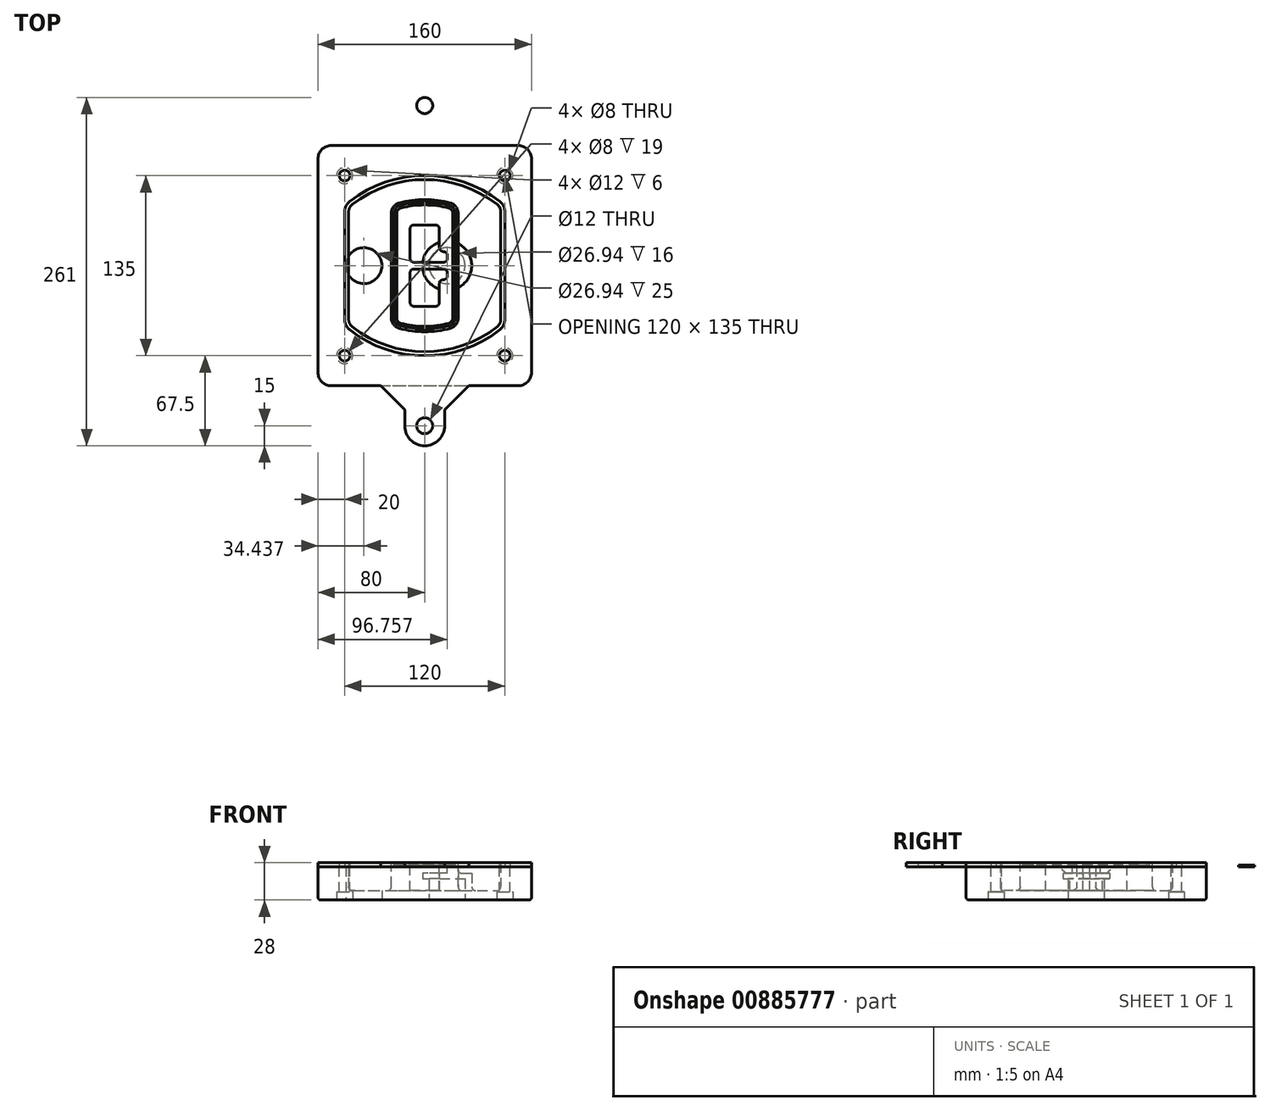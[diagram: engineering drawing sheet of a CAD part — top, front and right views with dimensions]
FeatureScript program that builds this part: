
annotation { "Feature Type Name" : "Feature", "Feature Type Description" : "" }
export const myFeature = defineFeature(function(context is Context, id is Id, definition is map)
    precondition{}
    {
        {
            var Q0;
            Q0=qCreatedBy(makeId("Top.planeOp"),FACE);
            var sketch = newSketch(context, id + "F0", { "sketchPlane" : qUnion([Q0])});
            skPoint(sketch, "E0.rect.middle", {"position": v(0, 0) * mm});
            skLineSegment(sketch, "E1.bottom", {"start": v(-70, -90) * mm, "end": v(70, -90) * mm});
            skLineSegment(sketch, "E1.top", {"start": v(-70, 90) * mm, "end": v(70, 90) * mm});
            skLineSegment(sketch, "E1.left", {"start": v(-80, -80) * mm, "end": v(-80, 80) * mm});
            skLineSegment(sketch, "E1.right", {"start": v(80, -80) * mm, "end": v(80, 80) * mm});
            skLineSegment(sketch, "E2", {"start": v(-80, 90) * mm, "end": v(80, -90) * mm, "construction": true});
            skLineSegment(sketch, "E3", {"start": v(80, 90) * mm, "end": v(-80, -90) * mm, "construction": true});
            skCircle(sketch, "E4", {"center": v(-60, 67.5) * mm, "radius": 4 * mm});
            skCircle(sketch, "E5", {"center": v(60, 67.5) * mm, "radius": 4 * mm});
            skCircle(sketch, "E6", {"center": v(60, -67.5) * mm, "radius": 4 * mm});
            skCircle(sketch, "E7", {"center": v(-60, -67.5) * mm, "radius": 4 * mm});
            skLineSegment(sketch, "E8", {"start": v(-60, 67.5) * mm, "end": v(60, 67.5) * mm, "construction": true});
            skLineSegment(sketch, "E9", {"start": v(60, 67.5) * mm, "end": v(60, -67.5) * mm, "construction": true});
            skLineSegment(sketch, "E10", {"start": v(60, -67.5) * mm, "end": v(-60, -67.5) * mm, "construction": true});
            skLineSegment(sketch, "E11", {"start": v(-60, -67.5) * mm, "end": v(-60, 67.5) * mm, "construction": true});
            skLineSegment(sketch, "E12", {"start": v(-60, 40.3) * mm, "end": v(-60, -40.3) * mm});
            skLineSegment(sketch, "E13", {"start": v(60, 40.3) * mm, "end": v(60, -40.3) * mm});
            skArc(sketch, "E14", {"start": v(56.15, 48.18) * mm, "mid": v(0, 67.5) * mm, "end": v(-56.15, 48.18) * mm});
            skArc(sketch, "E15", {"start": v(-56.15, -48.18) * mm, "mid": v(0, -67.5) * mm, "end": v(56.15, -48.18) * mm});
            skLineSegment(sketch, "E16", {"start": v(-60, 0) * mm, "end": v(60, 0) * mm, "construction": true});
            skPoint(sketch, "E17.visualSharp", {"position": v(-60, -45) * mm});
            skArc(sketch, "E17.filletArc", {"start": v(-60, -40.3) * mm, "mid": v(-58.99, -44.68) * mm, "end": v(-56.15, -48.18) * mm});
            skPoint(sketch, "E18.visualSharp", {"position": v(-60, 45) * mm});
            skArc(sketch, "E18.filletArc", {"start": v(-56.15, 48.18) * mm, "mid": v(-58.99, 44.68) * mm, "end": v(-60, 40.3) * mm});
            skPoint(sketch, "E19.visualSharp", {"position": v(60, 45) * mm});
            skArc(sketch, "E19.filletArc", {"start": v(60, 40.3) * mm, "mid": v(58.99, 44.68) * mm, "end": v(56.15, 48.18) * mm});
            skPoint(sketch, "E20.visualSharp", {"position": v(60, -45) * mm});
            skArc(sketch, "E20.filletArc", {"start": v(56.15, -48.18) * mm, "mid": v(58.99, -44.68) * mm, "end": v(60, -40.3) * mm});
            skPoint(sketch, "E21.visualSharp", {"position": v(-80, 90) * mm});
            skArc(sketch, "E21.filletArc", {"start": v(-70, 90) * mm, "mid": v(-77.07, 87.07) * mm, "end": v(-80, 80) * mm});
            skPoint(sketch, "E22.visualSharp", {"position": v(80, 90) * mm});
            skArc(sketch, "E22.filletArc", {"start": v(80, 80) * mm, "mid": v(77.07, 87.07) * mm, "end": v(70, 90) * mm});
            skPoint(sketch, "E23.visualSharp", {"position": v(80, -90) * mm});
            skArc(sketch, "E23.filletArc", {"start": v(70, -90) * mm, "mid": v(77.07, -87.07) * mm, "end": v(80, -80) * mm});
            skPoint(sketch, "E24.visualSharp", {"position": v(-80, -90) * mm});
            skArc(sketch, "E24.filletArc", {"start": v(-80, -80) * mm, "mid": v(-77.07, -87.07) * mm, "end": v(-70, -90) * mm});
            skArc(sketch, "E25.0", {"start": v(57, 40.3) * mm, "mid": v(56.3, 43.36) * mm, "end": v(54.3, 45.81) * mm});
            skLineSegment(sketch, "E25.1", {"start": v(57, 40.3) * mm, "end": v(57, -40.3) * mm});
            skArc(sketch, "E25.2", {"start": v(54.3, -45.81) * mm, "mid": v(56.3, -43.36) * mm, "end": v(57, -40.3) * mm});
            skArc(sketch, "E25.3", {"start": v(-54.3, -45.81) * mm, "mid": v(0, -64.5) * mm, "end": v(54.3, -45.81) * mm});
            skArc(sketch, "E25.4", {"start": v(-57, -40.3) * mm, "mid": v(-56.3, -43.36) * mm, "end": v(-54.3, -45.81) * mm});
            skArc(sketch, "E25.5", {"start": v(54.3, 45.81) * mm, "mid": v(0, 64.5) * mm, "end": v(-54.3, 45.81) * mm});
            skLineSegment(sketch, "E25.6", {"start": v(-57, 40.3) * mm, "end": v(-57, -40.3) * mm});
            skArc(sketch, "E25.7", {"start": v(-54.3, 45.81) * mm, "mid": v(-56.3, 43.36) * mm, "end": v(-57, 40.3) * mm});
            skArc(sketch, "E26.0", {"start": v(-58.62, 51.33) * mm, "mid": v(-62.58, 46.43) * mm, "end": v(-64, 40.3) * mm});
            skArc(sketch, "E26.1", {"start": v(58.62, 51.33) * mm, "mid": v(0, 71.5) * mm, "end": v(-58.62, 51.33) * mm});
            skArc(sketch, "E26.2", {"start": v(64, 40.3) * mm, "mid": v(62.58, 46.43) * mm, "end": v(58.62, 51.33) * mm});
            skLineSegment(sketch, "E26.3", {"start": v(64, 40.3) * mm, "end": v(64, -40.3) * mm});
            skArc(sketch, "E26.4", {"start": v(58.62, -51.33) * mm, "mid": v(62.58, -46.43) * mm, "end": v(64, -40.3) * mm});
            skLineSegment(sketch, "E26.5", {"start": v(-64, 40.3) * mm, "end": v(-64, -40.3) * mm});
            skArc(sketch, "E26.6", {"start": v(-58.62, -51.33) * mm, "mid": v(0, -71.5) * mm, "end": v(58.62, -51.33) * mm});
            skArc(sketch, "E26.7", {"start": v(-64, -40.3) * mm, "mid": v(-62.58, -46.43) * mm, "end": v(-58.62, -51.33) * mm});
            skSolve(sketch);
        }
        {
            var Q0;
            Q0=makeQuery(id+"F0.imprint","IMPRINT",FACE,{"disambiguationData":[TD([[makeQuery(id+"F0.imprint","IMPRINT",EDGE,{"derivedFrom":sQuery(id+"F0.wireOp",EDGE,"E1.bottom")}),1.0]])]});
            var Q1;
            Q1=makeQuery(id+"F0.imprint","IMPRINT",FACE,{"disambiguationData":[TD([[makeQuery(id+"F0.imprint","IMPRINT",EDGE,{"derivedFrom":sQuery(id+"F0.wireOp",EDGE,"E12")}),1.0]])]});
            var Q2;
            Q2=makeQuery(id+"F0.imprint","IMPRINT",FACE,{"disambiguationData":[TD([[makeQuery(id+"F0.imprint","IMPRINT",EDGE,{"derivedFrom":sQuery(id+"F0.wireOp",EDGE,"E25.0")}),1.0]])]});
            var Q3;
            Q3=makeQuery(id+"F0.imprint","IMPRINT",FACE,{"disambiguationData":[TD([[makeQuery(id+"F0.imprint","IMPRINT",EDGE,{"derivedFrom":sQuery(id+"F0.wireOp",EDGE,"E12")}),-1.0]])]});
            extrude(context, id + "F1", {"entities" : qUnion([Q0, Q1, Q2, Q3]), "oppositeDirection" : true, "depth" : 25 * mm});
        }
        {
            var Q0;
            Q0=makeQuery(id+"F0.imprint","IMPRINT",FACE,{"disambiguationData":[TD([[makeQuery(id+"F0.imprint","IMPRINT",EDGE,{"derivedFrom":sQuery(id+"F0.wireOp",EDGE,"E12")}),1.0]])]});
            extrude(context, id + "F2", {"entities" : qUnion([Q0]), "operationType" : NewBodyOperationType.ADD, "depth" : 3 * mm});
        }
        {
            var Q0;
            Q0=makeQuery(id+"F0.imprint","IMPRINT",FACE,{"disambiguationData":[TD([[makeQuery(id+"F0.imprint","IMPRINT",EDGE,{"derivedFrom":sQuery(id+"F0.wireOp",EDGE,"E25.0")}),1.0]])]});
            extrude(context, id + "F3", {"entities" : qUnion([Q0]), "operationType" : NewBodyOperationType.REMOVE, "oppositeDirection" : true, "depth" : 18 * mm});
        }
        {
            var Q0;
            Q0=makeQuery(id+"F2.opExtrude","CAP_FACE",FACE,{"disambiguationData":[OSD([sQuery(id+"F0.wireOp",EDGE,"E12"),sQuery(id+"F0.wireOp",EDGE,"E13"),sQuery(id+"F0.wireOp",EDGE,"E14"),sQuery(id+"F0.wireOp",EDGE,"E15"),sQuery(id+"F0.wireOp",EDGE,"E17.filletArc"),sQuery(id+"F0.wireOp",EDGE,"E18.filletArc"),sQuery(id+"F0.wireOp",EDGE,"E19.filletArc"),sQuery(id+"F0.wireOp",EDGE,"E20.filletArc"),sQuery(id+"F0.wireOp",EDGE,"E25.0"),sQuery(id+"F0.wireOp",EDGE,"E25.1"),sQuery(id+"F0.wireOp",EDGE,"E25.2"),sQuery(id+"F0.wireOp",EDGE,"E25.3"),sQuery(id+"F0.wireOp",EDGE,"E25.4"),sQuery(id+"F0.wireOp",EDGE,"E25.5"),sQuery(id+"F0.wireOp",EDGE,"E25.6"),sQuery(id+"F0.wireOp",EDGE,"E25.7")])],"isStart":false});
            var sketch = newSketch(context, id + "F4", { "sketchPlane" : qUnion([Q0])});
            skArc(sketch, "E27.0", {"start": v(-19.08, -46.97) * mm, "mid": v(0, -49.5) * mm, "end": v(19.08, -46.97) * mm});
            skArc(sketch, "E28.0", {"start": v(19.08, 46.97) * mm, "mid": v(0, 49.5) * mm, "end": v(-19.08, 46.97) * mm});
            skLineSegment(sketch, "E29", {"start": v(-25, 39.25) * mm, "end": v(-25, -39.25) * mm});
            skLineSegment(sketch, "E30", {"start": v(25, 39.25) * mm, "end": v(25, -39.25) * mm});
            skLineSegment(sketch, "E31", {"start": v(-25, 45.1) * mm, "end": v(25, 45.1) * mm, "construction": true});
            skLineSegment(sketch, "E32", {"start": v(-25, -45.1) * mm, "end": v(25, -45.1) * mm, "construction": true});
            skPoint(sketch, "E33.visualSharp", {"position": v(-25, 45.1) * mm});
            skArc(sketch, "E33.filletArc", {"start": v(-19.08, 46.97) * mm, "mid": v(-23.35, 44.11) * mm, "end": v(-25, 39.25) * mm});
            skPoint(sketch, "E34.visualSharp", {"position": v(25, 45.1) * mm});
            skArc(sketch, "E34.filletArc", {"start": v(25, 39.25) * mm, "mid": v(23.35, 44.11) * mm, "end": v(19.08, 46.97) * mm});
            skPoint(sketch, "E35.visualSharp", {"position": v(25, -45.1) * mm});
            skArc(sketch, "E35.filletArc", {"start": v(19.08, -46.97) * mm, "mid": v(23.35, -44.11) * mm, "end": v(25, -39.25) * mm});
            skPoint(sketch, "E36.visualSharp", {"position": v(-25, -45.1) * mm});
            skArc(sketch, "E36.filletArc", {"start": v(-25, -39.25) * mm, "mid": v(-23.35, -44.11) * mm, "end": v(-19.08, -46.97) * mm});
            skArc(sketch, "E37.0", {"start": v(54.3, 45.81) * mm, "mid": v(0, 64.5) * mm, "end": v(-54.3, 45.81) * mm});
            skArc(sketch, "E37.1", {"start": v(-54.3, 45.81) * mm, "mid": v(-56.3, 43.36) * mm, "end": v(-57, 40.3) * mm});
            skLineSegment(sketch, "E37.2", {"start": v(-57, 40.3) * mm, "end": v(-57, -40.3) * mm});
            skArc(sketch, "E37.3", {"start": v(-57, -40.3) * mm, "mid": v(-56.3, -43.36) * mm, "end": v(-54.3, -45.81) * mm});
            skArc(sketch, "E37.4", {"start": v(-54.3, -45.81) * mm, "mid": v(0, -64.5) * mm, "end": v(54.3, -45.81) * mm});
            skArc(sketch, "E37.5", {"start": v(54.3, -45.81) * mm, "mid": v(56.3, -43.36) * mm, "end": v(57, -40.3) * mm});
            skLineSegment(sketch, "E37.6", {"start": v(57, 40.3) * mm, "end": v(57, -40.3) * mm});
            skArc(sketch, "E37.7", {"start": v(57, 40.3) * mm, "mid": v(56.3, 43.36) * mm, "end": v(54.3, 45.81) * mm});
            skLineSegment(sketch, "E38.0", {"start": v(23, 39.25) * mm, "end": v(23, -39.25) * mm});
            skArc(sketch, "E38.1", {"start": v(18.56, -45.04) * mm, "mid": v(21.76, -42.9) * mm, "end": v(23, -39.25) * mm});
            skArc(sketch, "E38.2", {"start": v(-18.56, -45.04) * mm, "mid": v(0, -47.5) * mm, "end": v(18.56, -45.04) * mm});
            skArc(sketch, "E38.3", {"start": v(-23, -39.25) * mm, "mid": v(-21.76, -42.9) * mm, "end": v(-18.56, -45.04) * mm});
            skLineSegment(sketch, "E38.4", {"start": v(-23, 39.25) * mm, "end": v(-23, -39.25) * mm});
            skArc(sketch, "E38.5", {"start": v(23, 39.25) * mm, "mid": v(21.76, 42.9) * mm, "end": v(18.56, 45.04) * mm});
            skArc(sketch, "E38.6", {"start": v(-18.56, 45.04) * mm, "mid": v(-21.76, 42.9) * mm, "end": v(-23, 39.25) * mm});
            skArc(sketch, "E38.7", {"start": v(18.56, 45.04) * mm, "mid": v(0, 47.5) * mm, "end": v(-18.56, 45.04) * mm});
            skArc(sketch, "E39.0", {"start": v(21, 39.25) * mm, "mid": v(20.18, 41.68) * mm, "end": v(18.04, 43.1) * mm});
            skLineSegment(sketch, "E39.1", {"start": v(21, 39.25) * mm, "end": v(21, -39.25) * mm});
            skArc(sketch, "E39.2", {"start": v(18.04, -43.1) * mm, "mid": v(20.18, -41.68) * mm, "end": v(21, -39.25) * mm});
            skArc(sketch, "E39.3", {"start": v(-18.04, -43.1) * mm, "mid": v(0, -45.5) * mm, "end": v(18.04, -43.1) * mm});
            skArc(sketch, "E39.4", {"start": v(-21, -39.25) * mm, "mid": v(-20.18, -41.68) * mm, "end": v(-18.04, -43.1) * mm});
            skArc(sketch, "E39.5", {"start": v(18.04, 43.1) * mm, "mid": v(0, 45.5) * mm, "end": v(-18.04, 43.1) * mm});
            skLineSegment(sketch, "E39.6", {"start": v(-21, 39.25) * mm, "end": v(-21, -39.25) * mm});
            skArc(sketch, "E39.7", {"start": v(-18.04, 43.1) * mm, "mid": v(-20.18, 41.68) * mm, "end": v(-21, 39.25) * mm});
            skLineSegment(sketch, "E40", {"start": v(-25, 0) * mm, "end": v(25, 0) * mm, "construction": true});
            skLineSegment(sketch, "E41", {"start": v(-11, 5.5) * mm, "end": v(-11, 27.5) * mm});
            skLineSegment(sketch, "E42", {"start": v(-8, 30.5) * mm, "end": v(8, 30.5) * mm});
            skLineSegment(sketch, "E43", {"start": v(11, 27.5) * mm, "end": v(11, 13.5) * mm});
            skLineSegment(sketch, "E44", {"start": v(14, 10.5) * mm, "end": v(14, 10.5) * mm});
            skLineSegment(sketch, "E45", {"start": v(17, 7.5) * mm, "end": v(17, 5.5) * mm});
            skLineSegment(sketch, "E46", {"start": v(14, 2.5) * mm, "end": v(-8, 2.5) * mm});
            skPoint(sketch, "E47.visualSharp", {"position": v(-11, 30.5) * mm});
            skArc(sketch, "E47.filletArc", {"start": v(-8, 30.5) * mm, "mid": v(-10.12, 29.62) * mm, "end": v(-11, 27.5) * mm});
            skPoint(sketch, "E48.visualSharp", {"position": v(11, 30.5) * mm});
            skArc(sketch, "E48.filletArc", {"start": v(11, 27.5) * mm, "mid": v(10.12, 29.62) * mm, "end": v(8, 30.5) * mm});
            skPoint(sketch, "E49.visualSharp", {"position": v(11, 10.5) * mm});
            skArc(sketch, "E49.filletArc", {"start": v(11, 13.5) * mm, "mid": v(11.88, 11.38) * mm, "end": v(14, 10.5) * mm});
            skPoint(sketch, "E50.visualSharp", {"position": v(17, 10.5) * mm});
            skArc(sketch, "E50.filletArc", {"start": v(17, 7.5) * mm, "mid": v(16.12, 9.62) * mm, "end": v(14, 10.5) * mm});
            skPoint(sketch, "E51.visualSharp", {"position": v(17, 2.5) * mm});
            skArc(sketch, "E51.filletArc", {"start": v(14, 2.5) * mm, "mid": v(16.12, 3.38) * mm, "end": v(17, 5.5) * mm});
            skPoint(sketch, "E52.visualSharp", {"position": v(-11, 2.5) * mm});
            skArc(sketch, "E52.filletArc", {"start": v(-11, 5.5) * mm, "mid": v(-10.12, 3.38) * mm, "end": v(-8, 2.5) * mm});
            skLineSegment(sketch, "E53.0.MirrorCS", {"start": v(14, -2.5) * mm, "end": v(-8, -2.5) * mm});
            skArc(sketch, "E54.0.MirrorCS", {"start": v(-11, -5.5) * mm, "mid": v(-10.12, -3.38) * mm, "end": v(-8, -2.5) * mm});
            skLineSegment(sketch, "E55.0.MirrorCS", {"start": v(-11, -5.5) * mm, "end": v(-11, -27.5) * mm});
            skArc(sketch, "E56.0.MirrorCS", {"start": v(-8, -30.5) * mm, "mid": v(-10.12, -29.62) * mm, "end": v(-11, -27.5) * mm});
            skLineSegment(sketch, "E57.0.MirrorCS", {"start": v(-8, -30.5) * mm, "end": v(8, -30.5) * mm});
            skArc(sketch, "E58.0.MirrorCS", {"start": v(11, -27.5) * mm, "mid": v(10.12, -29.62) * mm, "end": v(8, -30.5) * mm});
            skLineSegment(sketch, "E59.0.MirrorCS", {"start": v(11, -27.5) * mm, "end": v(11, -13.5) * mm});
            skArc(sketch, "E60.0.MirrorCS", {"start": v(11, -13.5) * mm, "mid": v(11.88, -11.38) * mm, "end": v(14, -10.5) * mm});
            skArc(sketch, "E61.0.MirrorCS", {"start": v(17, -7.5) * mm, "mid": v(16.12, -9.62) * mm, "end": v(14, -10.5) * mm});
            skLineSegment(sketch, "E62.0.MirrorCS", {"start": v(17, -7.5) * mm, "end": v(17, -5.5) * mm});
            skArc(sketch, "E63.0.MirrorCS", {"start": v(14, -2.5) * mm, "mid": v(16.12, -3.38) * mm, "end": v(17, -5.5) * mm});
            skSolve(sketch);
        }
        {
            var Q0;
            Q0=makeQuery(id+"F4.imprint","IMPRINT",FACE,{"disambiguationData":[TD([[makeQuery(id+"F4.imprint","IMPRINT",EDGE,{"derivedFrom":sQuery(id+"F4.wireOp",EDGE,"E27.0")}),1.0]])]});
            var Q1;
            Q1=makeQuery(id+"F4.imprint","IMPRINT",FACE,{"disambiguationData":[TD([[makeQuery(id+"F4.imprint","IMPRINT",EDGE,{"derivedFrom":sQuery(id+"F4.wireOp",EDGE,"E38.0")}),-1.0]])]});
            var Q2;
            Q2=makeQuery(id+"F4.imprint","IMPRINT",FACE,{"disambiguationData":[TD([[makeQuery(id+"F4.imprint","IMPRINT",EDGE,{"derivedFrom":sQuery(id+"F4.wireOp",EDGE,"E39.0")}),1.0]])]});
            extrude(context, id + "F5", {"entities" : qUnion([Q0, Q1, Q2]), "operationType" : NewBodyOperationType.ADD, "endBound" : BoundingType.UP_TO_NEXT, "oppositeDirection" : true, "depth" : 25 * mm});
        }
        {
            var Q0;
            Q0=makeQuery(id+"F4.imprint","IMPRINT",FACE,{"disambiguationData":[TD([[makeQuery(id+"F4.imprint","IMPRINT",EDGE,{"derivedFrom":sQuery(id+"F4.wireOp",EDGE,"E38.0")}),-1.0]])]});
            extrude(context, id + "F6", {"entities" : qUnion([Q0]), "operationType" : NewBodyOperationType.REMOVE, "oppositeDirection" : true, "depth" : 2 * mm});
        }
        {
            var Q0;
            Q0=makeQuery(id+"F1.opExtrude","CAP_FACE",FACE,{"disambiguationData":[OSD([sQuery(id+"F0.wireOp",EDGE,"E1.bottom"),sQuery(id+"F0.wireOp",EDGE,"E1.top"),sQuery(id+"F0.wireOp",EDGE,"E1.left"),sQuery(id+"F0.wireOp",EDGE,"E1.right"),sQuery(id+"F0.wireOp",EDGE,"E4"),sQuery(id+"F0.wireOp",EDGE,"E5"),sQuery(id+"F0.wireOp",EDGE,"E6"),sQuery(id+"F0.wireOp",EDGE,"E7"),sQuery(id+"F0.wireOp",EDGE,"E21.filletArc"),sQuery(id+"F0.wireOp",EDGE,"E22.filletArc"),sQuery(id+"F0.wireOp",EDGE,"E23.filletArc"),sQuery(id+"F0.wireOp",EDGE,"E24.filletArc")])],"isStart":false});
            var sketch = newSketch(context, id + "F7", { "sketchPlane" : qUnion([Q0])});
            skCircle(sketch, "E64", {"center": v(16.76, 0) * mm, "radius": 13.47 * mm});
            skCircle(sketch, "E65", {"center": v(-45.56, 0) * mm, "radius": 13.47 * mm});
            skLineSegment(sketch, "E66", {"start": v(80, 0) * mm, "end": v(-80, 0) * mm});
            skCircle(sketch, "E67", {"center": v(16.76, 0) * mm, "radius": 18.47 * mm});
            skCircle(sketch, "E68", {"center": v(60, -67.5) * mm, "radius": 6 * mm});
            skCircle(sketch, "E69", {"center": v(-60, -67.5) * mm, "radius": 6 * mm});
            skCircle(sketch, "E70", {"center": v(-60, 67.5) * mm, "radius": 6 * mm});
            skCircle(sketch, "E71", {"center": v(60, 67.5) * mm, "radius": 6 * mm});
            skSolve(sketch);
        }
        {
            var Q0;
            {var subQ1=sQuery(id+"F7.wireOp",EDGE,"E66");var subQ4=sQuery(id+"F7.wireOp",EDGE,"E64");var subQ6=makeQuery(id+"F7.imprint","INTERSECT",VERTEX,{"disambiguationData":[OD(0.0)],"derivedFrom":[subQ4,subQ1]});Q0=makeQuery(id+"F7.imprint","IMPRINT",FACE,{"disambiguationData":[TD([[makeQuery(id+"F7.imprint","IMPRINT",EDGE,{"disambiguationData":[TD([[subQ6,-1.0]])],"derivedFrom":subQ4}),-1.0]])]});}
            var Q1;
            {var subQ0=sQuery(id+"F7.wireOp",EDGE,"E66");var subQ1=sQuery(id+"F7.wireOp",EDGE,"E64");var subQ3=makeQuery(id+"F7.imprint","INTERSECT",VERTEX,{"disambiguationData":[OD(0.0)],"derivedFrom":[subQ1,subQ0]});Q1=makeQuery(id+"F7.imprint","IMPRINT",FACE,{"disambiguationData":[TD([[makeQuery(id+"F7.imprint","IMPRINT",EDGE,{"disambiguationData":[TD([[subQ3,-1.0]])],"derivedFrom":subQ1}),1.0]])]});}
            var Q2;
            {var subQ0=sQuery(id+"F7.wireOp",EDGE,"E66");var subQ1=sQuery(id+"F7.wireOp",EDGE,"E64");var subQ3=makeQuery(id+"F7.imprint","INTERSECT",VERTEX,{"disambiguationData":[OD(0.0)],"derivedFrom":[subQ1,subQ0]});Q2=makeQuery(id+"F7.imprint","IMPRINT",FACE,{"disambiguationData":[TD([[makeQuery(id+"F7.imprint","IMPRINT",EDGE,{"disambiguationData":[TD([[subQ3,1.0]])],"derivedFrom":subQ1}),1.0]])]});}
            var Q3;
            {var subQ1=sQuery(id+"F7.wireOp",EDGE,"E66");var subQ4=sQuery(id+"F7.wireOp",EDGE,"E64");var subQ6=makeQuery(id+"F7.imprint","INTERSECT",VERTEX,{"disambiguationData":[OD(0.0)],"derivedFrom":[subQ4,subQ1]});Q3=makeQuery(id+"F7.imprint","IMPRINT",FACE,{"disambiguationData":[TD([[makeQuery(id+"F7.imprint","IMPRINT",EDGE,{"disambiguationData":[TD([[subQ6,1.0]])],"derivedFrom":subQ4}),-1.0]])]});}
            extrude(context, id + "F8", {"entities" : qUnion([Q0, Q1, Q2, Q3]), "operationType" : NewBodyOperationType.ADD, "oppositeDirection" : true, "depth" : 20 * mm});
        }
        {
            var Q0;
            {var subQ0=sQuery(id+"F7.wireOp",EDGE,"E66");var subQ1=sQuery(id+"F7.wireOp",EDGE,"E64");var subQ3=makeQuery(id+"F7.imprint","INTERSECT",VERTEX,{"disambiguationData":[OD(0.0)],"derivedFrom":[subQ1,subQ0]});Q0=makeQuery(id+"F7.imprint","IMPRINT",FACE,{"disambiguationData":[TD([[makeQuery(id+"F7.imprint","IMPRINT",EDGE,{"disambiguationData":[TD([[subQ3,-1.0]])],"derivedFrom":subQ1}),1.0]])]});}
            var Q1;
            {var subQ0=sQuery(id+"F7.wireOp",EDGE,"E66");var subQ1=sQuery(id+"F7.wireOp",EDGE,"E64");var subQ3=makeQuery(id+"F7.imprint","INTERSECT",VERTEX,{"disambiguationData":[OD(0.0)],"derivedFrom":[subQ1,subQ0]});Q1=makeQuery(id+"F7.imprint","IMPRINT",FACE,{"disambiguationData":[TD([[makeQuery(id+"F7.imprint","IMPRINT",EDGE,{"disambiguationData":[TD([[subQ3,1.0]])],"derivedFrom":subQ1}),1.0]])]});}
            extrude(context, id + "F9", {"entities" : qUnion([Q0, Q1]), "operationType" : NewBodyOperationType.REMOVE, "oppositeDirection" : true, "depth" : 16 * mm});
        }
        {
            var Q0;
            {var subQ0=sQuery(id+"F7.wireOp",EDGE,"E66");var subQ1=sQuery(id+"F7.wireOp",EDGE,"E65");var subQ3=makeQuery(id+"F7.imprint","INTERSECT",VERTEX,{"disambiguationData":[OD(0.0)],"derivedFrom":[subQ1,subQ0]});Q0=makeQuery(id+"F7.imprint","IMPRINT",FACE,{"disambiguationData":[TD([[makeQuery(id+"F7.imprint","IMPRINT",EDGE,{"disambiguationData":[TD([[subQ3,-1.0]])],"derivedFrom":subQ1}),1.0]])]});}
            var Q1;
            {var subQ0=sQuery(id+"F7.wireOp",EDGE,"E66");var subQ1=sQuery(id+"F7.wireOp",EDGE,"E65");var subQ3=makeQuery(id+"F7.imprint","INTERSECT",VERTEX,{"disambiguationData":[OD(0.0)],"derivedFrom":[subQ1,subQ0]});Q1=makeQuery(id+"F7.imprint","IMPRINT",FACE,{"disambiguationData":[TD([[makeQuery(id+"F7.imprint","IMPRINT",EDGE,{"disambiguationData":[TD([[subQ3,1.0]])],"derivedFrom":subQ1}),1.0]])]});}
            extrude(context, id + "F10", {"entities" : qUnion([Q0, Q1]), "operationType" : NewBodyOperationType.REMOVE, "oppositeDirection" : true, "depth" : 25 * mm});
        }
        {
            var Q0;
            Q0=makeQuery(id+"F7.imprint","IMPRINT",FACE,{"disambiguationData":[TD([[makeQuery(id+"F7.imprint","IMPRINT",EDGE,{"derivedFrom":sQuery(id+"F7.wireOp",EDGE,"E68")}),1.0]])]});
            var Q1;
            Q1=makeQuery(id+"F7.imprint","IMPRINT",FACE,{"disambiguationData":[TD([[makeQuery(id+"F7.imprint","IMPRINT",EDGE,{"derivedFrom":makeQuery(id+"F1.opExtrude","CAP_EDGE",EDGE,{"disambiguationData":[OSD([sQuery(id+"F0.wireOp",EDGE,"E5")])],"isStart":false})}),-1.0]])]});
            var Q2;
            Q2=makeQuery(id+"F7.imprint","IMPRINT",FACE,{"disambiguationData":[TD([[makeQuery(id+"F7.imprint","IMPRINT",EDGE,{"derivedFrom":sQuery(id+"F7.wireOp",EDGE,"E69")}),1.0]])]});
            var Q3;
            Q3=makeQuery(id+"F7.imprint","IMPRINT",FACE,{"disambiguationData":[TD([[makeQuery(id+"F7.imprint","IMPRINT",EDGE,{"derivedFrom":makeQuery(id+"F1.opExtrude","CAP_EDGE",EDGE,{"disambiguationData":[OSD([sQuery(id+"F0.wireOp",EDGE,"E4")])],"isStart":false})}),-1.0]])]});
            var Q4;
            Q4=makeQuery(id+"F7.imprint","IMPRINT",FACE,{"disambiguationData":[TD([[makeQuery(id+"F7.imprint","IMPRINT",EDGE,{"derivedFrom":sQuery(id+"F7.wireOp",EDGE,"E70")}),1.0]])]});
            var Q5;
            Q5=makeQuery(id+"F7.imprint","IMPRINT",FACE,{"disambiguationData":[TD([[makeQuery(id+"F7.imprint","IMPRINT",EDGE,{"derivedFrom":makeQuery(id+"F1.opExtrude","CAP_EDGE",EDGE,{"disambiguationData":[OSD([sQuery(id+"F0.wireOp",EDGE,"E7")])],"isStart":false})}),-1.0]])]});
            var Q6;
            Q6=makeQuery(id+"F7.imprint","IMPRINT",FACE,{"disambiguationData":[TD([[makeQuery(id+"F7.imprint","IMPRINT",EDGE,{"derivedFrom":sQuery(id+"F7.wireOp",EDGE,"E71")}),1.0]])]});
            var Q7;
            Q7=makeQuery(id+"F7.imprint","IMPRINT",FACE,{"disambiguationData":[TD([[makeQuery(id+"F7.imprint","IMPRINT",EDGE,{"derivedFrom":makeQuery(id+"F1.opExtrude","CAP_EDGE",EDGE,{"disambiguationData":[OSD([sQuery(id+"F0.wireOp",EDGE,"E6")])],"isStart":false})}),-1.0]])]});
            extrude(context, id + "F11", {"entities" : qUnion([Q0, Q1, Q2, Q3, Q4, Q5, Q6, Q7]), "operationType" : NewBodyOperationType.REMOVE, "oppositeDirection" : true, "depth" : 6 * mm});
        }
        {
            var Q0;
            Q0=makeQuery(id+"F9.boolean.opBoolean","COPY",FACE,{"derivedFrom":makeQuery(id+"F9.opExtrude","CAP_FACE",FACE,{"disambiguationData":[OSD([sQuery(id+"F7.wireOp",EDGE,"E64")])],"isStart":false})});
            var sketch = newSketch(context, id + "F12", { "sketchPlane" : qUnion([Q0])});
            skArc(sketch, "E72.0", {"start": v(11, 17.55) * mm, "mid": v(2.57, 11.82) * mm, "end": v(-1.54, 2.5) * mm});
            skArc(sketch, "E72.1", {"start": v(-1.54, -2.5) * mm, "mid": v(2.57, -11.82) * mm, "end": v(11, -17.55) * mm});
            skLineSegment(sketch, "E73", {"start": v(-1.54, -2.5) * mm, "end": v(14, -2.5) * mm});
            skLineSegment(sketch, "E74.0", {"start": v(14, 2.5) * mm, "end": v(-1.54, 2.5) * mm});
            skArc(sketch, "E74.1", {"start": v(14, 2.5) * mm, "mid": v(16.12, 3.38) * mm, "end": v(17, 5.5) * mm});
            skLineSegment(sketch, "E74.2", {"start": v(17, 7.5) * mm, "end": v(17, 5.5) * mm});
            skArc(sketch, "E74.3", {"start": v(17, 7.5) * mm, "mid": v(16.12, 9.62) * mm, "end": v(14, 10.5) * mm});
            skArc(sketch, "E74.4", {"start": v(11, 13.5) * mm, "mid": v(11.88, 11.38) * mm, "end": v(14, 10.5) * mm});
            skLineSegment(sketch, "E74.5", {"start": v(11, 17.55) * mm, "end": v(11, 13.5) * mm});
            skLineSegment(sketch, "E74.7", {"start": v(14, -2.5) * mm, "end": v(-1.54, -2.5) * mm});
            skArc(sketch, "E74.8", {"start": v(14, -2.5) * mm, "mid": v(16.12, -3.38) * mm, "end": v(17, -5.5) * mm});
            skLineSegment(sketch, "E74.9", {"start": v(17, -7.5) * mm, "end": v(17, -5.5) * mm});
            skArc(sketch, "E74.10", {"start": v(17, -7.5) * mm, "mid": v(16.12, -9.62) * mm, "end": v(14, -10.5) * mm});
            skArc(sketch, "E74.11", {"start": v(11, -13.5) * mm, "mid": v(11.88, -11.38) * mm, "end": v(14, -10.5) * mm});
            skLineSegment(sketch, "E74.12", {"start": v(11, -17.55) * mm, "end": v(11, -13.5) * mm});
            skPoint(sketch, "E75.orphan", {"position": v(11, -27.5) * mm});
            skPoint(sketch, "E76.orphan", {"position": v(-8, -2.5) * mm});
            skPoint(sketch, "E77.orphan", {"position": v(-8, 2.5) * mm});
            skPoint(sketch, "E78.orphan", {"position": v(11, 27.5) * mm});
            skSolve(sketch);
        }
        {
            var Q0;
            {var subQ7=sQuery(id+"F12.wireOp",EDGE,"E72.0");var subQ14=sQuery(id+"F12.wireOp",EDGE,"E72.1");var subQ16=sQuery(id+"F12.wireOp",EDGE,"E74.1");var subQ18=sQuery(id+"F12.wireOp",EDGE,"E74.8");Q0=qUnion([makeQuery(id+"F12.imprint","IMPRINT",FACE,{"disambiguationData":[TD([[makeQuery(id+"F12.imprint","IMPRINT",EDGE,{"derivedFrom":subQ7}),1.0]])]}),makeQuery(id+"F12.imprint","IMPRINT",FACE,{"disambiguationData":[TD([[makeQuery(id+"F12.imprint","IMPRINT",EDGE,{"derivedFrom":subQ14}),1.0]])]}),makeQuery(id+"F12.imprint","IMPRINT",FACE,{"disambiguationData":[TD([[makeQuery(id+"F12.imprint","IMPRINT",EDGE,{"derivedFrom":subQ16}),1.0]])]}),makeQuery(id+"F12.imprint","IMPRINT",FACE,{"disambiguationData":[TD([[makeQuery(id+"F12.imprint","IMPRINT",EDGE,{"derivedFrom":subQ18}),-1.0]])]})]);}
            var Q1;
            Q1=makeQuery(id+"F5.boolean.opBoolean","SPLIT",FACE,{"disambiguationData":[TD([makeQuery(id+"F5.opExtrude","SWEPT_FACE",FACE,{"disambiguationData":[OSD([sQuery(id+"F4.wireOp",EDGE,"E41")])]})])],"derivedFrom":makeQuery(id+"F3.boolean.opBoolean","COPY",FACE,{"derivedFrom":makeQuery(id+"F3.opExtrude","CAP_FACE",FACE,{"disambiguationData":[OSD([sQuery(id+"F0.wireOp",EDGE,"E25.0"),sQuery(id+"F0.wireOp",EDGE,"E25.1"),sQuery(id+"F0.wireOp",EDGE,"E25.2"),sQuery(id+"F0.wireOp",EDGE,"E25.3"),sQuery(id+"F0.wireOp",EDGE,"E25.4"),sQuery(id+"F0.wireOp",EDGE,"E25.5"),sQuery(id+"F0.wireOp",EDGE,"E25.6"),sQuery(id+"F0.wireOp",EDGE,"E25.7")])],"isStart":false})})});
            extrude(context, id + "F13", {"entities" : qUnion([Q0]), "operationType" : NewBodyOperationType.REMOVE, "endBound" : BoundingType.UP_TO_SURFACE, "endBoundEntityFace" : qUnion([Q1]), "depth" : 25 * mm});
        }
        {
            var Q0;
            Q0=makeQuery(id+"F3.boolean.opBoolean","COPY",EDGE,{"derivedFrom":makeQuery(id+"F3.opExtrude","CAP_EDGE",EDGE,{"disambiguationData":[OSD([sQuery(id+"F0.wireOp",EDGE,"E25.6")])],"isStart":false})});
            var Q1;
            Q1=makeQuery(id+"F8.boolean.opBoolean","INTERSECT",EDGE,{"derivedFrom":[makeQuery(id+"F5.opExtrude","SWEPT_FACE",FACE,{"disambiguationData":[OSD([sQuery(id+"F4.wireOp",EDGE,"E30")])]}),makeQuery(id+"F8.opExtrude","CAP_FACE",FACE,{"disambiguationData":[OSD([sQuery(id+"F7.wireOp",EDGE,"E67")])],"isStart":false})]});
            var Q2;
            Q2=makeQuery(id+"F8.boolean.opBoolean","INTERSECT",EDGE,{"disambiguationData":[OD(1.0)],"derivedFrom":[makeQuery(id+"F5.opExtrude","SWEPT_FACE",FACE,{"disambiguationData":[OSD([sQuery(id+"F4.wireOp",EDGE,"E30")])]}),makeQuery(id+"F8.opExtrude","SWEPT_FACE",FACE,{"disambiguationData":[OSD([sQuery(id+"F7.wireOp",EDGE,"E67")])]})]});
            var Q3;
            {var subQ0=sQuery(id+"F4.wireOp",EDGE,"E30");Q3=makeQuery(id+"F8.boolean.opBoolean","SPLIT",EDGE,{"disambiguationData":[TD([makeQuery(id+"F5.opExtrude","SWEPT_FACE",FACE,{"disambiguationData":[OSD([sQuery(id+"F4.wireOp",EDGE,"E35.filletArc")])]})])],"derivedFrom":makeQuery(id+"F5.opExtrude","CAP_EDGE",EDGE,{"disambiguationData":[OSD([subQ0])],"isStart":false})});}
            var Q4;
            {var subQ0=sQuery(id+"F0.wireOp",EDGE,"E25.7");var subQ1=sQuery(id+"F0.wireOp",EDGE,"E25.1");var subQ2=sQuery(id+"F0.wireOp",EDGE,"E25.6");var subQ3=sQuery(id+"F0.wireOp",EDGE,"E25.5");var subQ4=sQuery(id+"F0.wireOp",EDGE,"E25.4");var subQ5=sQuery(id+"F0.wireOp",EDGE,"E25.0");var subQ6=sQuery(id+"F0.wireOp",EDGE,"E25.2");var subQ7=sQuery(id+"F0.wireOp",EDGE,"E25.3");Q4=makeQuery(id+"F8.boolean.opBoolean","INTERSECT",EDGE,{"derivedFrom":[makeQuery(id+"F5.boolean.opBoolean","SPLIT",FACE,{"disambiguationData":[TD([makeQuery(id+"F2.opExtrude","SWEPT_FACE",FACE,{"disambiguationData":[OSD([subQ5])]})])],"derivedFrom":makeQuery(id+"F3.boolean.opBoolean","COPY",FACE,{"derivedFrom":makeQuery(id+"F3.opExtrude","CAP_FACE",FACE,{"disambiguationData":[OSD([subQ5,subQ1,subQ6,subQ7,subQ4,subQ3,subQ2,subQ0])],"isStart":false})})}),makeQuery(id+"F8.opExtrude","SWEPT_FACE",FACE,{"disambiguationData":[OSD([sQuery(id+"F7.wireOp",EDGE,"E67")])]})]});}
            var Q5;
            Q5=makeQuery(id+"F8.boolean.opBoolean","INTERSECT",EDGE,{"disambiguationData":[OD(0.0)],"derivedFrom":[makeQuery(id+"F5.opExtrude","SWEPT_FACE",FACE,{"disambiguationData":[OSD([sQuery(id+"F4.wireOp",EDGE,"E30")])]}),makeQuery(id+"F8.opExtrude","SWEPT_FACE",FACE,{"disambiguationData":[OSD([sQuery(id+"F7.wireOp",EDGE,"E67")])]})]});
            fillet(context, id + "F14", {"entities" : qUnion([Q0, Q1, Q2, Q3, Q4, Q5]), "radius" : 3 * mm, "tangentPropagation" : true, "allowEdgeOverflow" : false});
        }
        {
            var Q0;
            Q0=makeQuery(id+"F1.opExtrude","CAP_EDGE",EDGE,{"disambiguationData":[OSD([sQuery(id+"F0.wireOp",EDGE,"E1.bottom")])],"isStart":false});
            fillet(context, id + "F15", {"entities" : qUnion([Q0]), "radius" : 2 * mm, "tangentPropagation" : true, "allowEdgeOverflow" : false});
        }
        {
            var Q0;
            {var subQ0=sQuery(id+"F0.wireOp",EDGE,"E21.filletArc");var subQ1=sQuery(id+"F0.wireOp",EDGE,"E7");var subQ2=sQuery(id+"F0.wireOp",EDGE,"E6");var subQ3=sQuery(id+"F0.wireOp",EDGE,"E5");var subQ4=sQuery(id+"F0.wireOp",EDGE,"E4");var subQ5=sQuery(id+"F0.wireOp",EDGE,"E22.filletArc");var subQ6=sQuery(id+"F0.wireOp",EDGE,"E1.bottom");var subQ7=sQuery(id+"F0.wireOp",EDGE,"E1.right");var subQ8=sQuery(id+"F0.wireOp",EDGE,"E1.top");var subQ9=sQuery(id+"F0.wireOp",EDGE,"E1.left");var subQ10=sQuery(id+"F0.wireOp",EDGE,"E23.filletArc");var subQ11=sQuery(id+"F0.wireOp",EDGE,"E24.filletArc");Q0=makeQuery(id+"F2.boolean.opBoolean","SPLIT",FACE,{"disambiguationData":[TD([makeQuery(id+"F1.opExtrude","SWEPT_FACE",FACE,{"disambiguationData":[OSD([subQ6])]})])],"derivedFrom":makeQuery(id+"F1.opExtrude","CAP_FACE",FACE,{"disambiguationData":[OSD([subQ6,subQ8,subQ9,subQ7,subQ4,subQ3,subQ2,subQ1,subQ0,subQ5,subQ10,subQ11])],"isStart":true})});}
            var sketch = newSketch(context, id + "F16", { "sketchPlane" : qUnion([Q0])});
            skArc(sketch, "E79.0", {"start": v(-70, 90) * mm, "mid": v(-77.07, 87.07) * mm, "end": v(-80, 80) * mm});
            skLineSegment(sketch, "E79.1", {"start": v(-70, 90) * mm, "end": v(70, 90) * mm});
            skArc(sketch, "E79.2", {"start": v(80, 80) * mm, "mid": v(77.07, 87.07) * mm, "end": v(70, 90) * mm});
            skLineSegment(sketch, "E79.3", {"start": v(80, -80) * mm, "end": v(80, 80) * mm});
            skArc(sketch, "E79.4", {"start": v(70, -90) * mm, "mid": v(77.07, -87.07) * mm, "end": v(80, -80) * mm});
            skLineSegment(sketch, "E79.5", {"start": v(-70, -90) * mm, "end": v(70, -90) * mm});
            skArc(sketch, "E79.6", {"start": v(-80, -80) * mm, "mid": v(-77.07, -87.07) * mm, "end": v(-70, -90) * mm});
            skLineSegment(sketch, "E79.7", {"start": v(-80, -80) * mm, "end": v(-80, 80) * mm});
            skCircle(sketch, "E79.8", {"center": v(-60, -67.5) * mm, "radius": 4 * mm});
            skCircle(sketch, "E79.9", {"center": v(-60, 67.5) * mm, "radius": 4 * mm});
            skCircle(sketch, "E79.10", {"center": v(60, 67.5) * mm, "radius": 4 * mm});
            skCircle(sketch, "E79.11", {"center": v(60, -67.5) * mm, "radius": 4 * mm});
            skArc(sketch, "E79.12", {"start": v(-56.15, -48.18) * mm, "mid": v(0, -67.5) * mm, "end": v(56.15, -48.18) * mm});
            skArc(sketch, "E79.13", {"start": v(56.15, -48.18) * mm, "mid": v(58.99, -44.68) * mm, "end": v(60, -40.3) * mm});
            skLineSegment(sketch, "E79.14", {"start": v(60, 40.3) * mm, "end": v(60, -40.3) * mm});
            skArc(sketch, "E79.15", {"start": v(60, 40.3) * mm, "mid": v(58.99, 44.68) * mm, "end": v(56.15, 48.18) * mm});
            skArc(sketch, "E79.16", {"start": v(56.15, 48.18) * mm, "mid": v(0, 67.5) * mm, "end": v(-56.15, 48.18) * mm});
            skArc(sketch, "E79.17", {"start": v(-56.15, 48.18) * mm, "mid": v(-58.99, 44.68) * mm, "end": v(-60, 40.3) * mm});
            skLineSegment(sketch, "E79.18", {"start": v(-60, 40.3) * mm, "end": v(-60, -40.3) * mm});
            skArc(sketch, "E79.19", {"start": v(-60, -40.3) * mm, "mid": v(-58.99, -44.68) * mm, "end": v(-56.15, -48.18) * mm});
            skLineSegment(sketch, "E80", {"start": v(0, 90) * mm, "end": v(0, 120) * mm, "construction": true});
            skArc(sketch, "E81", {"start": v(-15, 120) * mm, "mid": v(0, 135) * mm, "end": v(15, 120) * mm});
            skLineSegment(sketch, "E82", {"start": v(-15, 120) * mm, "end": v(-15, 108) * mm});
            skLineSegment(sketch, "E83", {"start": v(-15, 108) * mm, "end": v(-33, 90) * mm});
            skLineSegment(sketch, "E84", {"start": v(15, 120) * mm, "end": v(15, 108) * mm});
            skPoint(sketch, "E84.endSnap0", {"position": v(0, 105) * mm});
            skLineSegment(sketch, "E85", {"start": v(15, 108) * mm, "end": v(33, 90) * mm});
            skCircle(sketch, "E86", {"center": v(0, 120) * mm, "radius": 6 * mm});
            skLineSegment(sketch, "E87", {"start": v(-80, 0) * mm, "end": v(80, 0) * mm, "construction": true});
            skLineSegment(sketch, "E88.MirrorCS", {"start": v(15, -108) * mm, "end": v(33, -90) * mm});
            skLineSegment(sketch, "E89.MirrorCS", {"start": v(15, -120) * mm, "end": v(15, -108) * mm});
            skArc(sketch, "E90.MirrorCS", {"start": v(-15, -120) * mm, "mid": v(0, -135) * mm, "end": v(15, -120) * mm});
            skCircle(sketch, "E91.MirrorC", {"center": v(0, -120) * mm, "radius": 6 * mm});
            skLineSegment(sketch, "E92.MirrorCS", {"start": v(0, -90) * mm, "end": v(0, -120) * mm, "construction": true});
            skLineSegment(sketch, "E93.MirrorCS", {"start": v(-15, -120) * mm, "end": v(-15, -108) * mm});
            skLineSegment(sketch, "E94.MirrorCS", {"start": v(-15, -108) * mm, "end": v(-33, -90) * mm});
            skLineSegment(sketch, "E95", {"start": v(-15, 120) * mm, "end": v(0, 120) * mm, "construction": true});
            skLineSegment(sketch, "E96", {"start": v(0, 120) * mm, "end": v(15, 120) * mm, "construction": true});
            skSolve(sketch);
        }
        {
            var Q0;
            Q0=makeQuery(id+"F16.imprint","IMPRINT",FACE,{"disambiguationData":[TD([[makeQuery(id+"F16.imprint","IMPRINT",EDGE,{"derivedFrom":sQuery(id+"F16.wireOp",EDGE,"E81")}),-1.0]])]});
            var Q1;
            {var subQ0=sQuery(id+"F16.wireOp",EDGE,"E88.MirrorCS");Q1=makeQuery(id+"F16.imprint","IMPRINT",FACE,{"disambiguationData":[TD([[makeQuery(id+"F16.imprint","IMPRINT",EDGE,{"derivedFrom":subQ0}),1.0]])]});}
            var Q2;
            {var subQ5=sQuery(id+"F16.wireOp",EDGE,"E79.0");Q2=makeQuery(id+"F16.imprint","IMPRINT",FACE,{"disambiguationData":[TD([[makeQuery(id+"F16.imprint","IMPRINT",EDGE,{"derivedFrom":subQ5}),1.0]])]});}
            var Q3;
            Q3=makeQuery(id+"F2.opExtrude","CAP_FACE",FACE,{"disambiguationData":[OSD([sQuery(id+"F0.wireOp",EDGE,"E12"),sQuery(id+"F0.wireOp",EDGE,"E13"),sQuery(id+"F0.wireOp",EDGE,"E14"),sQuery(id+"F0.wireOp",EDGE,"E15"),sQuery(id+"F0.wireOp",EDGE,"E17.filletArc"),sQuery(id+"F0.wireOp",EDGE,"E18.filletArc"),sQuery(id+"F0.wireOp",EDGE,"E19.filletArc"),sQuery(id+"F0.wireOp",EDGE,"E20.filletArc"),sQuery(id+"F0.wireOp",EDGE,"E25.0"),sQuery(id+"F0.wireOp",EDGE,"E25.1"),sQuery(id+"F0.wireOp",EDGE,"E25.2"),sQuery(id+"F0.wireOp",EDGE,"E25.3"),sQuery(id+"F0.wireOp",EDGE,"E25.4"),sQuery(id+"F0.wireOp",EDGE,"E25.5"),sQuery(id+"F0.wireOp",EDGE,"E25.6"),sQuery(id+"F0.wireOp",EDGE,"E25.7")])],"isStart":false});
            extrude(context, id + "F17", {"entities" : qUnion([Q0, Q1, Q2]), "endBound" : BoundingType.UP_TO_SURFACE, "depth" : 25 * mm, "endBoundEntityFace" : qUnion([Q3]), "offsetDistance" : 25 * mm});
        }
        {
            var Q0;
            Q0=makeQuery(id+"F16.imprint","IMPRINT",FACE,{"disambiguationData":[TD([[makeQuery(id+"F16.imprint","IMPRINT",EDGE,{"derivedFrom":sQuery(id+"F16.wireOp",EDGE,"E86")}),1.0]])]});
            var Q1;
            Q1=makeQuery(id+"F2.opExtrude","CAP_FACE",FACE,{"disambiguationData":[OSD([sQuery(id+"F0.wireOp",EDGE,"E12"),sQuery(id+"F0.wireOp",EDGE,"E13"),sQuery(id+"F0.wireOp",EDGE,"E14"),sQuery(id+"F0.wireOp",EDGE,"E15"),sQuery(id+"F0.wireOp",EDGE,"E17.filletArc"),sQuery(id+"F0.wireOp",EDGE,"E18.filletArc"),sQuery(id+"F0.wireOp",EDGE,"E19.filletArc"),sQuery(id+"F0.wireOp",EDGE,"E20.filletArc"),sQuery(id+"F0.wireOp",EDGE,"E25.0"),sQuery(id+"F0.wireOp",EDGE,"E25.1"),sQuery(id+"F0.wireOp",EDGE,"E25.2"),sQuery(id+"F0.wireOp",EDGE,"E25.3"),sQuery(id+"F0.wireOp",EDGE,"E25.4"),sQuery(id+"F0.wireOp",EDGE,"E25.5"),sQuery(id+"F0.wireOp",EDGE,"E25.6"),sQuery(id+"F0.wireOp",EDGE,"E25.7")])],"isStart":false});
            extrude(context, id + "F18", {"entities" : qUnion([Q0]), "operationType" : NewBodyOperationType.ADD, "endBound" : BoundingType.UP_TO_SURFACE, "depth" : 25 * mm, "endBoundEntityFace" : qUnion([Q1]), "hasOffset" : true, "offsetDistance" : 2 * mm});
        }
        {
            var Q0;
            Q0=makeQuery(id+"F1.opExtrude","SWEPT_FACE",FACE,{"disambiguationData":[OSD([sQuery(id+"F0.wireOp",EDGE,"E1.right")])]});
            var sketch = newSketch(context, id + "F19", { "sketchPlane" : qUnion([Q0])});
            skLineSegment(sketch, "E97.bottom", {"start": v(96.86, 13.79) * mm, "end": v(117.04, 13.79) * mm});
            skLineSegment(sketch, "E97.top", {"start": v(96.86, -41.74) * mm, "end": v(117.04, -41.74) * mm});
            skLineSegment(sketch, "E97.left", {"start": v(96.86, 13.79) * mm, "end": v(96.86, -41.74) * mm});
            skLineSegment(sketch, "E97.right", {"start": v(117.04, 13.79) * mm, "end": v(117.04, -41.74) * mm});
            skLineSegment(sketch, "E98", {"start": v(127.36, 17.25) * mm, "end": v(127.36, -64.92) * mm, "construction": true});
            skSolve(sketch);
        }
        {
            var Q0;
            Q0=makeQuery(id+"F19.imprint","IMPRINT",FACE,{"disambiguationData":[TD([[makeQuery(id+"F19.imprint","IMPRINT",EDGE,{"derivedFrom":sQuery(id+"F19.wireOp",EDGE,"E97.bottom")}),-1.0]])]});
            var Q1;
            Q1=sQuery(id+"F19.wireOp",EDGE,"E97.left");
            var Q2;
            Q2=sQuery(id+"F19.wireOp",EDGE,"E97.right");
            var Q3;
            Q3=sQuery(id+"F19.wireOp",EDGE,"E97.top");
            var Q4;
            Q4=sQuery(id+"F19.wireOp",EDGE,"E98");
            revolve(context, id + "F20", {"bodyType" : ToolBodyType.SURFACE, "surfaceOperationType" : NewSurfaceOperationType.NEW, "entities" : qUnion([Q0]), "surfaceEntities" : qUnion([Q1, Q2, Q3]), "axis" : qUnion([Q4]), "revolveType" : RevolveType.TWO_DIRECTIONS, "angle" : 30 * degree, "angleBack" : 270 * degree});
        }
    });
